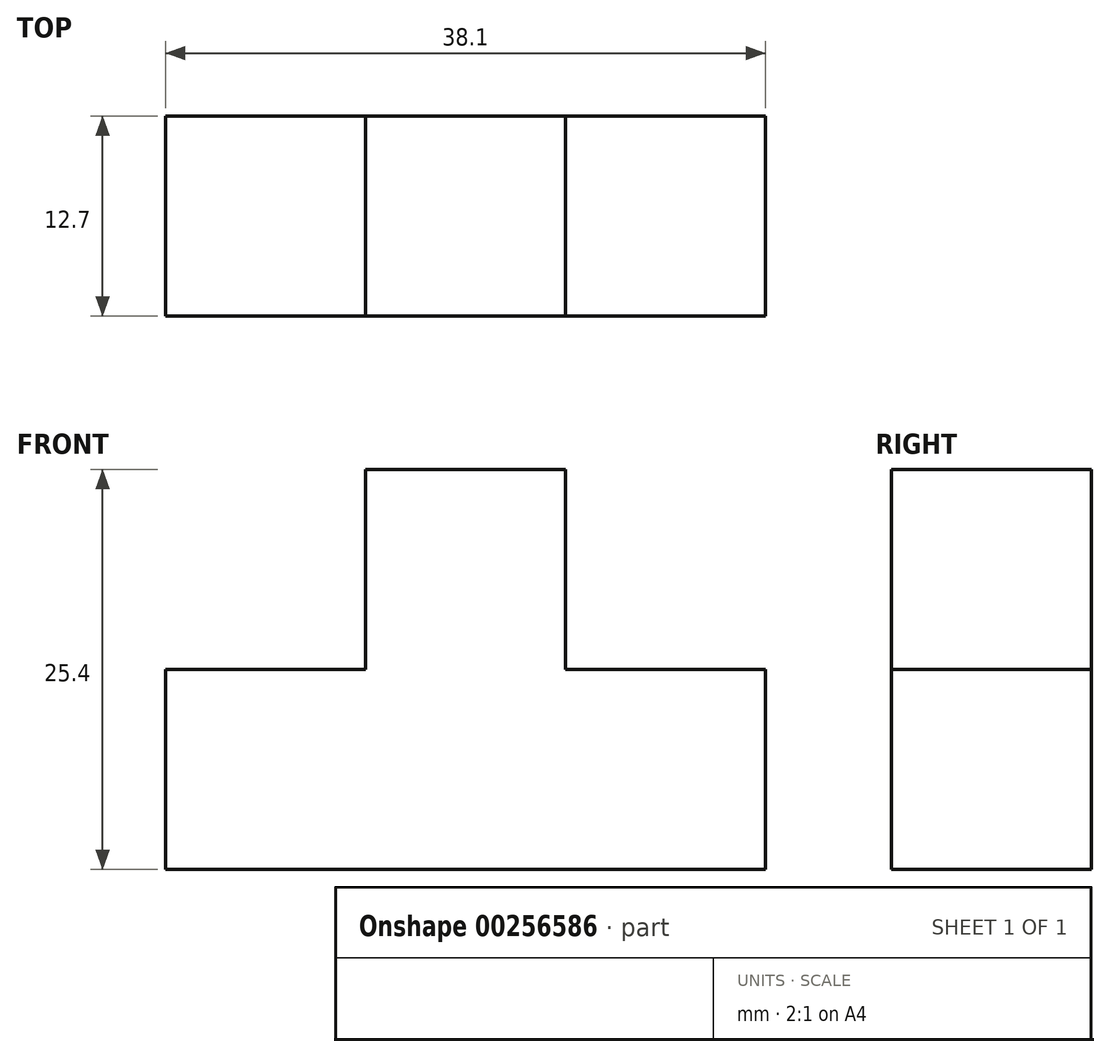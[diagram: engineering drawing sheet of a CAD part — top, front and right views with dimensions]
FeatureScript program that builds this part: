
annotation { "Feature Type Name" : "Feature", "Feature Type Description" : "" }
export const myFeature = defineFeature(function(context is Context, id is Id, definition is map)
    precondition{}
    {
        {
            var Q0;
            Q0=qCreatedBy(makeId("Front.planeOp"),FACE);
            var sketch = newSketch(context, id + "F0", { "sketchPlane" : qUnion([Q0])});
            skLineSegment(sketch, "E0", {"start": v(0, 0) * mm, "end": v(38.1, 0) * mm});
            skLineSegment(sketch, "E1", {"start": v(38.1, 0) * mm, "end": v(38.1, 12.7) * mm});
            skLineSegment(sketch, "E2", {"start": v(38.1, 12.7) * mm, "end": v(25.4, 12.7) * mm});
            skLineSegment(sketch, "E3", {"start": v(25.4, 12.7) * mm, "end": v(25.4, 25.4) * mm});
            skLineSegment(sketch, "E4", {"start": v(25.4, 25.4) * mm, "end": v(12.7, 25.4) * mm});
            skLineSegment(sketch, "E5", {"start": v(12.7, 25.4) * mm, "end": v(12.7, 12.7) * mm});
            skLineSegment(sketch, "E6", {"start": v(12.7, 12.7) * mm, "end": v(0, 12.7) * mm});
            skLineSegment(sketch, "E7", {"start": v(0, 12.7) * mm, "end": v(0, 0) * mm});
            skSolve(sketch);
        }
        {
            var Q0;
            Q0 = qSketchRegion(id + "F0", true);
            extrude(context, id + "F1", {"entities" : qUnion([Q0]), "depth" : 12.7 * mm});
        }
    });
